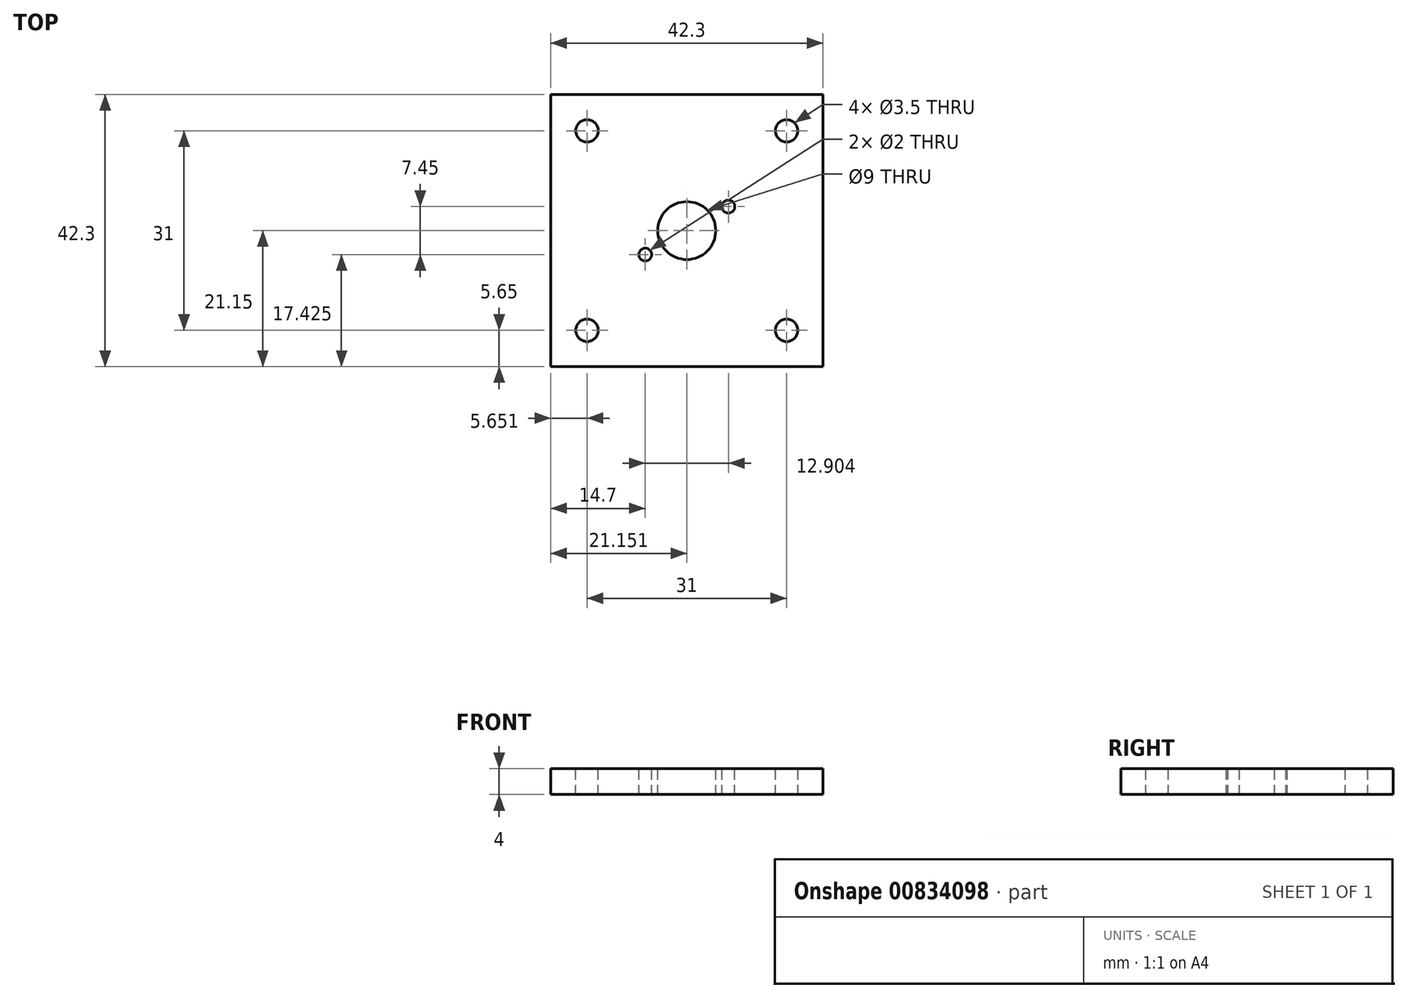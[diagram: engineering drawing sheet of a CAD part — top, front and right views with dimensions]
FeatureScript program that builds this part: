
annotation { "Feature Type Name" : "Feature", "Feature Type Description" : "" }
export const myFeature = defineFeature(function(context is Context, id is Id, definition is map)
    precondition{}
    {
        {
            var Q0;
            Q0=qCreatedBy(makeId("Top.planeOp"),FACE);
            var sketch = newSketch(context, id + "F0", { "sketchPlane" : qUnion([Q0])});
            skLineSegment(sketch, "E0.bottom", {"start": v(-22.2, 20.42) * mm, "end": v(20.1, 20.42) * mm});
            skLineSegment(sketch, "E0.top", {"start": v(-22.2, -21.88) * mm, "end": v(20.1, -21.88) * mm});
            skLineSegment(sketch, "E0.left", {"start": v(-22.2, 20.42) * mm, "end": v(-22.2, -21.88) * mm});
            skLineSegment(sketch, "E0.right", {"start": v(20.1, 20.42) * mm, "end": v(20.1, -21.88) * mm});
            skSolve(sketch);
        }
        {
            var Q0;
            Q0=makeQuery(id+"F0.imprint","IMPRINT",FACE,{"disambiguationData":[TD([[makeQuery(id+"F0.imprint","IMPRINT",EDGE,{"derivedFrom":sQuery(id+"F0.wireOp",EDGE,"E0.bottom")}),-1.0]])]});
            extrude(context, id + "F1", {"entities" : qUnion([Q0]), "depth" : 4 * mm, "offsetDistance" : 25 * mm});
        }
        {
            var Q0;
            Q0=makeQuery(id+"F1.opExtrude","CAP_FACE",FACE,{"disambiguationData":[OSD([sQuery(id+"F0.wireOp",EDGE,"E0.bottom"),sQuery(id+"F0.wireOp",EDGE,"E0.top"),sQuery(id+"F0.wireOp",EDGE,"E0.left"),sQuery(id+"F0.wireOp",EDGE,"E0.right")])],"isStart":false});
            var sketch = newSketch(context, id + "F2", { "sketchPlane" : qUnion([Q0])});
            skCircle(sketch, "E1", {"center": v(-16.55, -16.23) * mm, "radius": 1.75 * mm});
            skCircle(sketch, "E2", {"center": v(14.45, -16.23) * mm, "radius": 1.75 * mm});
            skCircle(sketch, "E3", {"center": v(14.45, 14.77) * mm, "radius": 1.75 * mm});
            skCircle(sketch, "E4", {"center": v(-16.55, 14.77) * mm, "radius": 1.75 * mm});
            skCircle(sketch, "E5", {"center": v(-1.05, -0.73) * mm, "radius": 4.5 * mm});
            skCircle(sketch, "E6", {"center": v(-7.5, -4.46) * mm, "radius": 1 * mm});
            skCircle(sketch, "E7", {"center": v(5.4, 3) * mm, "radius": 1 * mm});
            skSolve(sketch);
        }
        {
            var Q0;
            Q0 = qSketchRegion(id + "F2", true);
            extrude(context, id + "F3", {"entities" : qUnion([Q0]), "operationType" : NewBodyOperationType.REMOVE, "oppositeDirection" : true, "depth" : 25 * mm, "offsetDistance" : 25 * mm});
        }
    });
